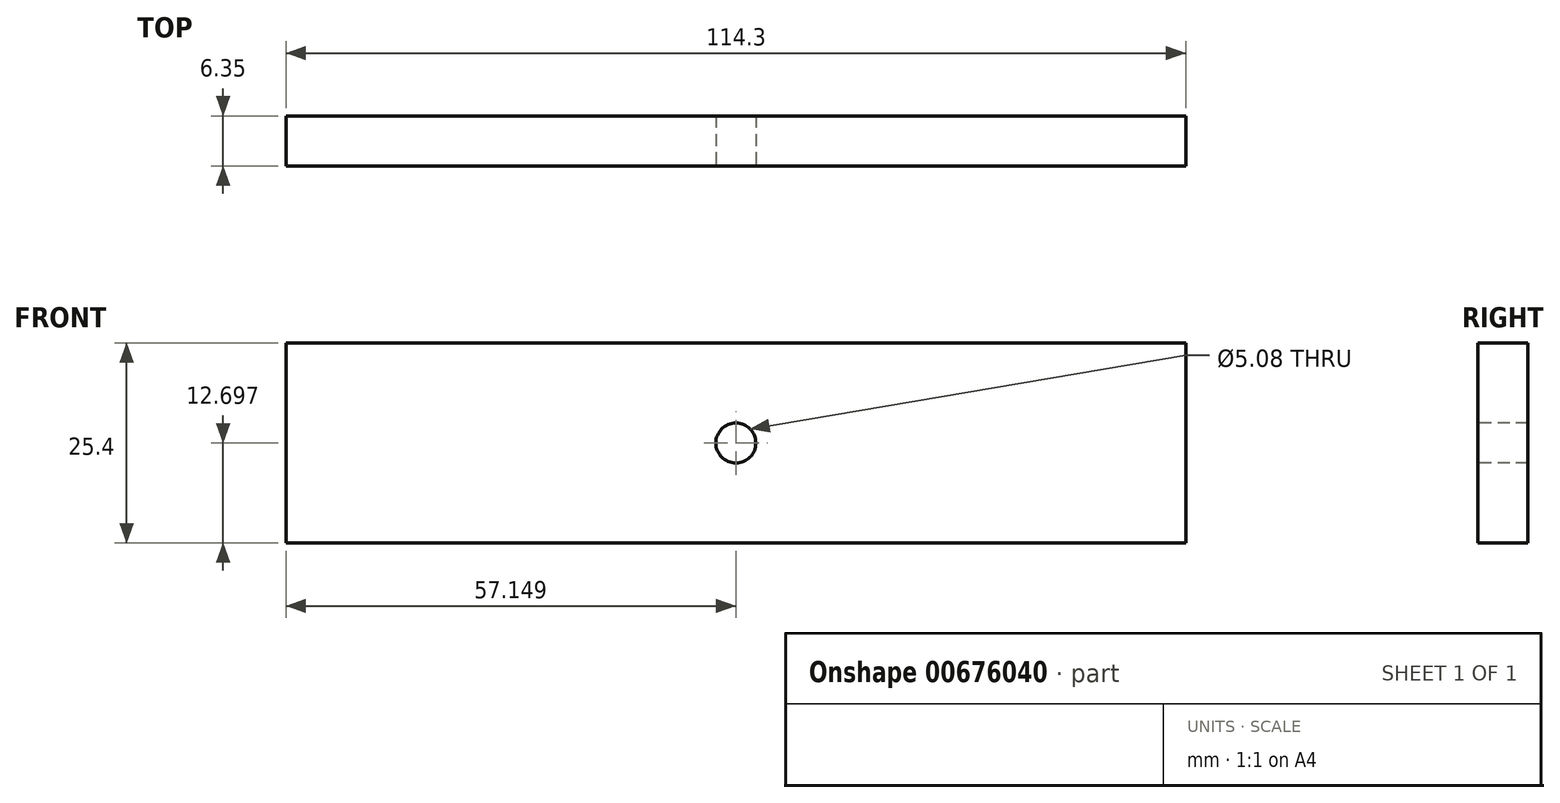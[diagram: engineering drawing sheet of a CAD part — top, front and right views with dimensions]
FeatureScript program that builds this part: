
annotation { "Feature Type Name" : "Feature", "Feature Type Description" : "" }
export const myFeature = defineFeature(function(context is Context, id is Id, definition is map)
    precondition{}
    {
        {
            var Q0;
            Q0=qCreatedBy(makeId("Front.planeOp"),FACE);
            var sketch = newSketch(context, id + "F0", { "sketchPlane" : qUnion([Q0])});
            skLineSegment(sketch, "E0.bottom", {"start": v(-68.13, 34.59) * mm, "end": v(46.17, 34.59) * mm});
            skLineSegment(sketch, "E0.top", {"start": v(-68.13, 9.19) * mm, "end": v(46.17, 9.19) * mm});
            skLineSegment(sketch, "E0.left", {"start": v(-68.13, 34.59) * mm, "end": v(-68.13, 9.19) * mm});
            skLineSegment(sketch, "E0.right", {"start": v(46.17, 34.59) * mm, "end": v(46.17, 9.19) * mm});
            skSolve(sketch);
        }
        {
            var Q0;
            Q0 = qSketchRegion(id + "F0", true);
            extrude(context, id + "F1", {"entities" : qUnion([Q0]), "depth" : 6.35 * mm, "offsetDistance" : 25.4 * mm});
        }
        {
            var Q0;
            Q0=makeQuery(id+"F1.opExtrude","CAP_FACE",FACE,{"disambiguationData":[OSD([sQuery(id+"F0.wireOp",EDGE,"E0.bottom"),sQuery(id+"F0.wireOp",EDGE,"E0.top"),sQuery(id+"F0.wireOp",EDGE,"E0.left"),sQuery(id+"F0.wireOp",EDGE,"E0.right")])],"isStart":false});
            var sketch = newSketch(context, id + "F2", { "sketchPlane" : qUnion([Q0])});
            skCircle(sketch, "E1", {"center": v(-10.98, 21.89) * mm, "radius": 2.54 * mm});
            skPoint(sketch, "E1.centerSnap0", {"position": v(-68.13, 21.89) * mm});
            skSolve(sketch);
        }
        {
            var Q0;
            Q0=sQuery(id+"F2.wireOp",VERTEX,"E1.center");
            var Q1;
            Q1=makeQuery(id+"F1.opExtrude","SWEPT_BODY",BODY,{"disambiguationData":[OSD([sQuery(id+"F0.wireOp",EDGE,"E0.bottom"),sQuery(id+"F0.wireOp",EDGE,"E0.top"),sQuery(id+"F0.wireOp",EDGE,"E0.left"),sQuery(id+"F0.wireOp",EDGE,"E0.right")])]});
            hole(context, id + "F3", {"style" : HoleStyle.SIMPLE, "endStyle" : HoleEndStyle.THROUGH, "holeDiameter" : 5.08 * mm, "majorDiameter" : 6.35 * mm, "isTappedThrough" : true, "tappedDepth" : 12.7 * mm, "tapClearance" : 3, "locations" : qUnion([Q0]), "scope" : qUnion([Q1])});
        }
    });
